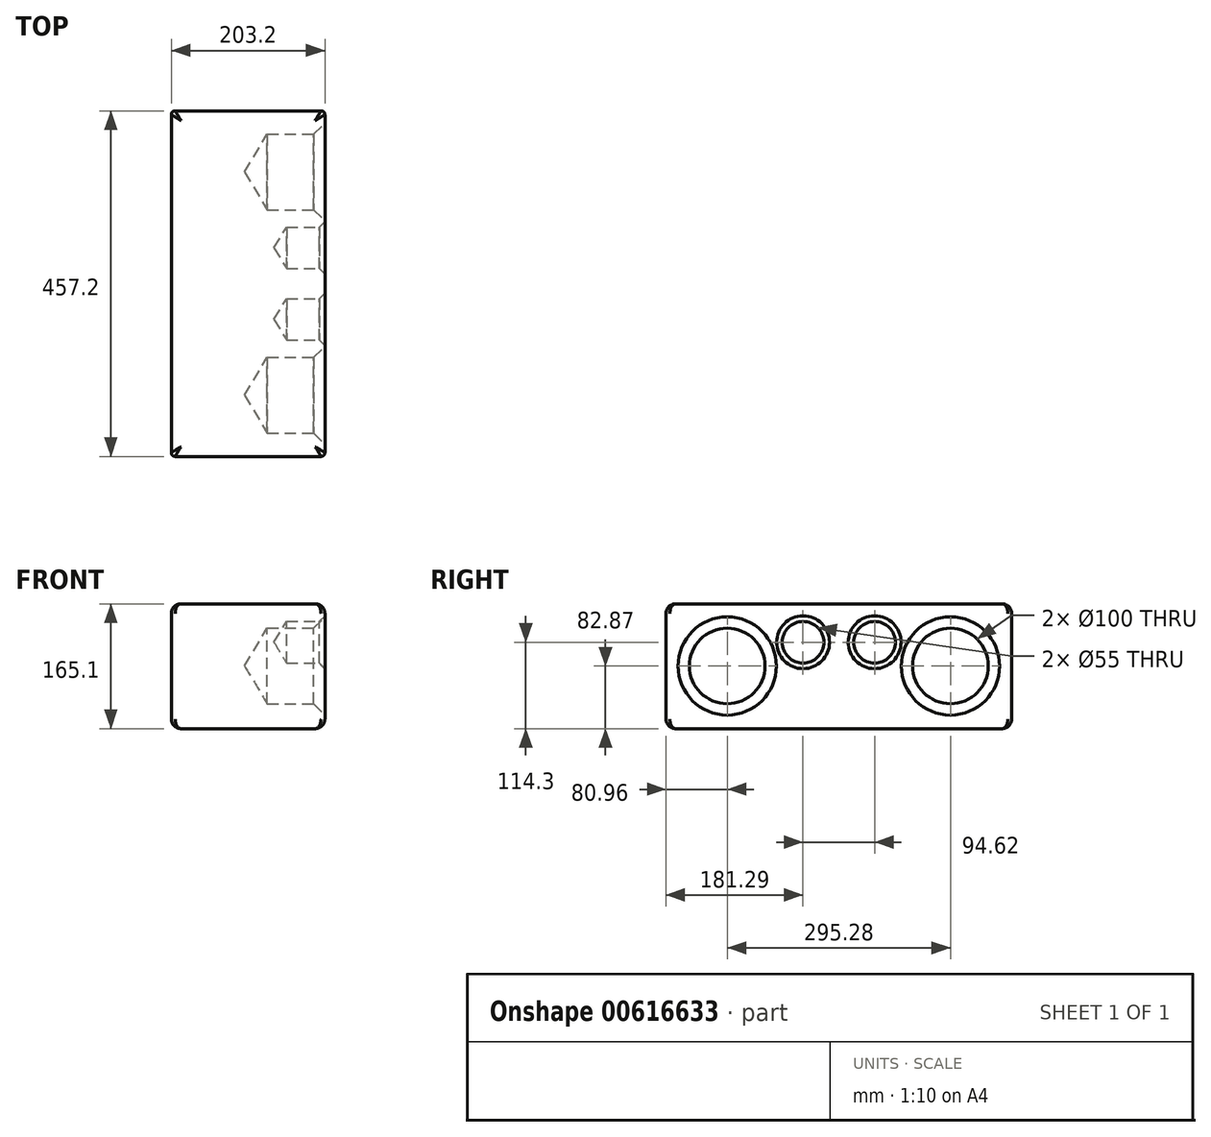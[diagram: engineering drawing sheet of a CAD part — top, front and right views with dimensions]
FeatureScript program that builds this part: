
annotation { "Feature Type Name" : "Feature", "Feature Type Description" : "" }
export const myFeature = defineFeature(function(context is Context, id is Id, definition is map)
    precondition{}
    {
        {
            var Q0;
            Q0=qCreatedBy(makeId("Right.planeOp"),FACE);
            var sketch = newSketch(context, id + "F0", { "sketchPlane" : qUnion([Q0])});
            skLineSegment(sketch, "E0.bottom", {"start": v(0, 0) * mm, "end": v(457.2, 0) * mm});
            skLineSegment(sketch, "E0.top", {"start": v(0, 165.1) * mm, "end": v(457.2, 165.1) * mm});
            skLineSegment(sketch, "E0.left", {"start": v(0, 0) * mm, "end": v(0, 165.1) * mm});
            skLineSegment(sketch, "E0.right", {"start": v(457.2, 0) * mm, "end": v(457.2, 165.1) * mm});
            skSolve(sketch);
        }
        {
            var Q0;
            Q0=makeQuery(id+"F0.imprint","IMPRINT",FACE,{"disambiguationData":[TD([[makeQuery(id+"F0.imprint","IMPRINT",EDGE,{"derivedFrom":sQuery(id+"F0.wireOp",EDGE,"E0.bottom")}),1.0]])]});
            extrude(context, id + "F1", {"entities" : qUnion([Q0]), "depth" : 203.2 * mm, "offsetDistance" : 25.4 * mm});
        }
        {
            var Q0;
            Q0=makeQuery(id+"F1.opExtrude","SWEPT_EDGE",EDGE,{"disambiguationData":[OSD([sQuery(id+"F0.wireOp",EDGE,"E0.top"),sQuery(id+"F0.wireOp",EDGE,"E0.left")])]});
            var Q1;
            Q1=makeQuery(id+"F1.opExtrude","SWEPT_EDGE",EDGE,{"disambiguationData":[OSD([sQuery(id+"F0.wireOp",EDGE,"E0.top"),sQuery(id+"F0.wireOp",EDGE,"E0.right")])]});
            var Q2;
            Q2=makeQuery(id+"F1.opExtrude","CAP_EDGE",EDGE,{"disambiguationData":[OSD([sQuery(id+"F0.wireOp",EDGE,"E0.top")])],"isStart":true});
            var Q3;
            Q3=makeQuery(id+"F1.opExtrude","CAP_EDGE",EDGE,{"disambiguationData":[OSD([sQuery(id+"F0.wireOp",EDGE,"E0.top")])],"isStart":false});
            fillet(context, id + "F2", {"entities" : qUnion([Q0, Q1, Q2, Q3]), "radius" : 12.7 * mm, "tangentPropagation" : true, "allowEdgeOverflow" : false});
        }
        {
            var Q0;
            Q0=makeQuery(id+"F1.opExtrude","CAP_EDGE",EDGE,{"disambiguationData":[OSD([sQuery(id+"F0.wireOp",EDGE,"E0.bottom")])],"isStart":false});
            var Q1;
            Q1=makeQuery(id+"F1.opExtrude","CAP_EDGE",EDGE,{"disambiguationData":[OSD([sQuery(id+"F0.wireOp",EDGE,"E0.bottom")])],"isStart":true});
            var Q2;
            Q2=makeQuery(id+"F1.opExtrude","SWEPT_EDGE",EDGE,{"disambiguationData":[OSD([sQuery(id+"F0.wireOp",EDGE,"E0.bottom"),sQuery(id+"F0.wireOp",EDGE,"E0.right")])]});
            var Q3;
            Q3=makeQuery(id+"F1.opExtrude","SWEPT_EDGE",EDGE,{"disambiguationData":[OSD([sQuery(id+"F0.wireOp",EDGE,"E0.bottom"),sQuery(id+"F0.wireOp",EDGE,"E0.left")])]});
            fillet(context, id + "F3", {"entities" : qUnion([Q0, Q1, Q2, Q3]), "radius" : 12.7 * mm, "tangentPropagation" : true, "allowEdgeOverflow" : false});
        }
        {
            var Q0;
            Q0=makeQuery(id+"F1.opExtrude","CAP_EDGE",EDGE,{"disambiguationData":[OSD([sQuery(id+"F0.wireOp",EDGE,"E0.left")])],"isStart":false});
            var Q1;
            Q1=makeQuery(id+"F1.opExtrude","CAP_EDGE",EDGE,{"disambiguationData":[OSD([sQuery(id+"F0.wireOp",EDGE,"E0.right")])],"isStart":false});
            var Q2;
            Q2=makeQuery(id+"F1.opExtrude","CAP_EDGE",EDGE,{"disambiguationData":[OSD([sQuery(id+"F0.wireOp",EDGE,"E0.right")])],"isStart":true});
            var Q3;
            Q3=makeQuery(id+"F1.opExtrude","CAP_EDGE",EDGE,{"disambiguationData":[OSD([sQuery(id+"F0.wireOp",EDGE,"E0.left")])],"isStart":true});
            fillet(context, id + "F4", {"entities" : qUnion([Q0, Q1, Q2, Q3]), "radius" : 5.08 * mm, "tangentPropagation" : true, "allowEdgeOverflow" : false});
        }
        {
            var Q0;
            Q0=makeQuery(id+"F1.opExtrude","CAP_FACE",FACE,{"disambiguationData":[OSD([sQuery(id+"F0.wireOp",EDGE,"E0.bottom"),sQuery(id+"F0.wireOp",EDGE,"E0.top"),sQuery(id+"F0.wireOp",EDGE,"E0.left"),sQuery(id+"F0.wireOp",EDGE,"E0.right")])],"isStart":false});
            var sketch = newSketch(context, id + "F5", { "sketchPlane" : qUnion([Q0])});
            skPoint(sketch, "E1", {"position": v(80.96, 82.87) * mm});
            skPoint(sketch, "E2", {"position": v(376.24, 82.87) * mm});
            skPoint(sketch, "E3", {"position": v(181.3, 114.3) * mm});
            skPoint(sketch, "E4", {"position": v(275.9, 114.3) * mm});
            skSolve(sketch);
        }
        {
            var Q0;
            Q0=sQuery(id+"F5.wireOp",VERTEX,"E1");
            var Q1;
            Q1=makeQuery(id+"F1.opExtrude","SWEPT_BODY",BODY,{"disambiguationData":[OSD([sQuery(id+"F0.wireOp",EDGE,"E0.bottom"),sQuery(id+"F0.wireOp",EDGE,"E0.top"),sQuery(id+"F0.wireOp",EDGE,"E0.left"),sQuery(id+"F0.wireOp",EDGE,"E0.right")])]});
            hole(context, id + "F6", {"style" : HoleStyle.C_SINK, "endStyle" : HoleEndStyle.BLIND, "holeDiameter" : 100 * mm, "cSinkDiameter" : 130 * mm, "cSinkAngle" : 90 * degree, "majorDiameter" : 6.35 * mm, "holeDepth" : 76.2 * mm, "isTappedThrough" : true, "tappedDepth" : 12.7 * mm, "tapClearance" : 3, "locations" : qUnion([Q0]), "scope" : qUnion([Q1])});
        }
        {
            var Q0;
            Q0=sQuery(id+"F5.wireOp",VERTEX,"E2");
            var Q1;
            Q1=makeQuery(id+"F1.opExtrude","SWEPT_BODY",BODY,{"disambiguationData":[OSD([sQuery(id+"F0.wireOp",EDGE,"E0.bottom"),sQuery(id+"F0.wireOp",EDGE,"E0.top"),sQuery(id+"F0.wireOp",EDGE,"E0.left"),sQuery(id+"F0.wireOp",EDGE,"E0.right")])]});
            hole(context, id + "F7", {"style" : HoleStyle.C_SINK, "endStyle" : HoleEndStyle.BLIND, "holeDiameter" : 100 * mm, "cSinkDiameter" : 130 * mm, "cSinkAngle" : 90 * degree, "majorDiameter" : 6.35 * mm, "holeDepth" : 76.2 * mm, "isTappedThrough" : true, "tappedDepth" : 12.7 * mm, "tapClearance" : 3, "locations" : qUnion([Q0]), "scope" : qUnion([Q1])});
        }
        {
            var Q0;
            Q0=sQuery(id+"F5.wireOp",VERTEX,"E3");
            var Q1;
            Q1=sQuery(id+"F5.wireOp",VERTEX,"E4");
            var Q2;
            Q2=makeQuery(id+"F1.opExtrude","SWEPT_BODY",BODY,{"disambiguationData":[OSD([sQuery(id+"F0.wireOp",EDGE,"E0.bottom"),sQuery(id+"F0.wireOp",EDGE,"E0.top"),sQuery(id+"F0.wireOp",EDGE,"E0.left"),sQuery(id+"F0.wireOp",EDGE,"E0.right")])]});
            hole(context, id + "F8", {"style" : HoleStyle.C_SINK, "endStyle" : HoleEndStyle.BLIND, "holeDiameter" : 55 * mm, "cSinkDiameter" : 70 * mm, "cSinkAngle" : 90 * degree, "majorDiameter" : 6.35 * mm, "holeDepth" : 50.8 * mm, "isTappedThrough" : true, "tappedDepth" : 12.7 * mm, "tapClearance" : 3, "locations" : qUnion([Q0, Q1]), "scope" : qUnion([Q2])});
        }
    });
